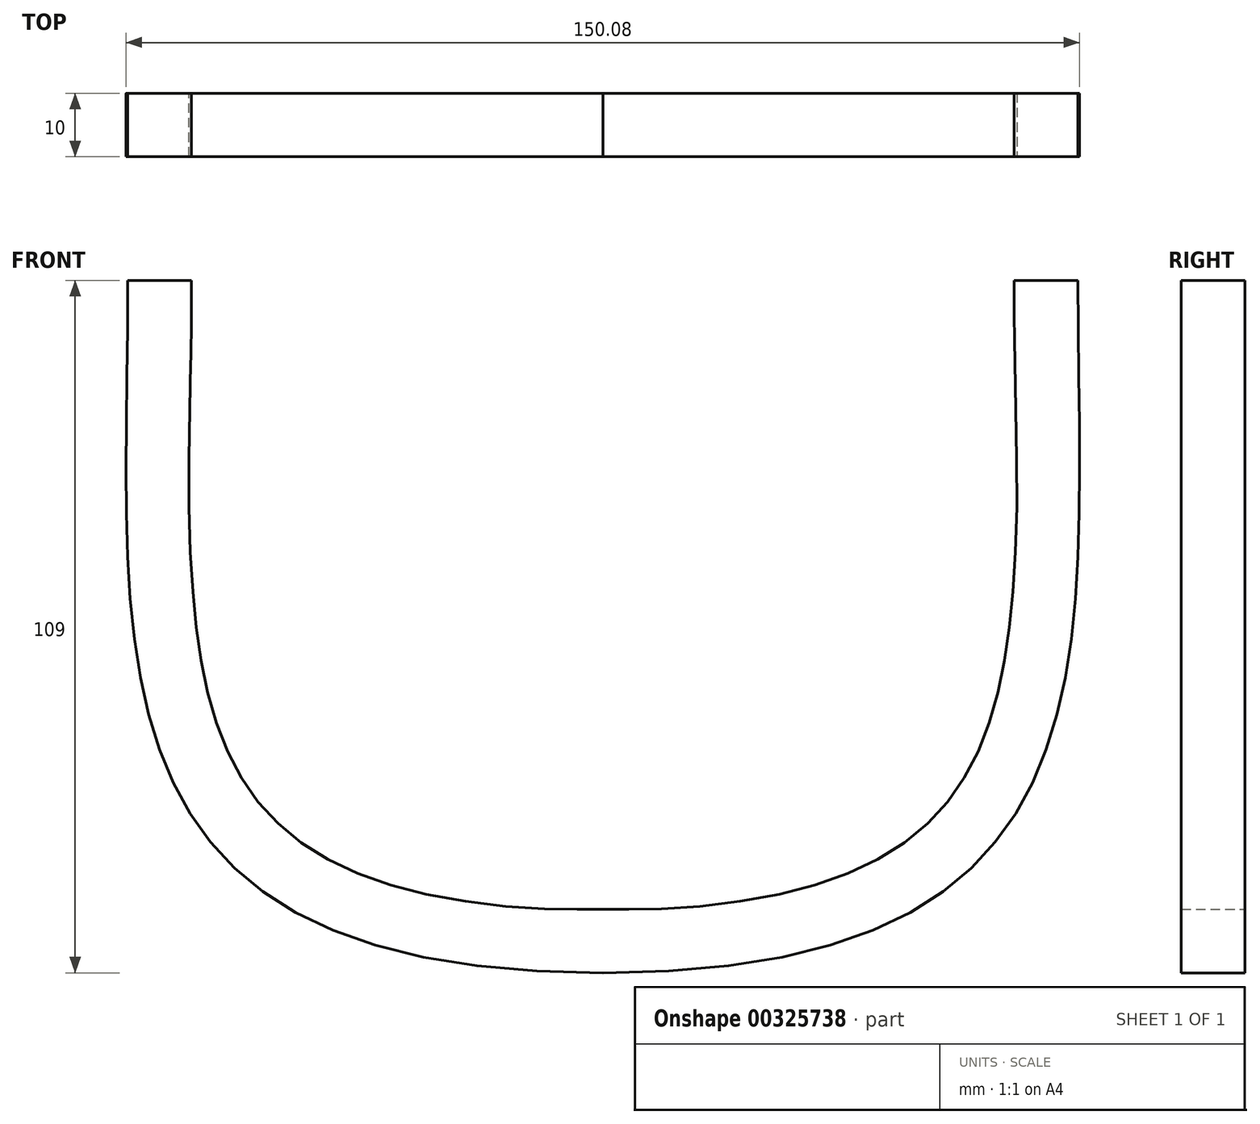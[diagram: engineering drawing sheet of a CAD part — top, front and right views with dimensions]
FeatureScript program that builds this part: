
annotation { "Feature Type Name" : "Feature", "Feature Type Description" : "" }
export const myFeature = defineFeature(function(context is Context, id is Id, definition is map)
    precondition{}
    {
        {
            var Q0;
            Q0=qCreatedBy(makeId("Front.planeOp"),FACE);
            var sketch = newSketch(context, id + "F0", { "sketchPlane" : qUnion([Q0])});
            skLineSegment(sketch, "E0", {"start": v(-75.24, 0) * mm, "end": v(74.76, 0) * mm, "construction": true});
            skLineSegment(sketch, "E1", {"start": v(74.76, 0) * mm, "end": v(74.76, 109) * mm, "construction": true});
            skLineSegment(sketch, "E2", {"start": v(0, 0) * mm, "end": v(0, 109) * mm, "construction": true});
            skFitSpline(sketch, "E3", {"points": [v(0, 0) * mm, v(74.76, 109) * mm], "startDerivative": vector(251, 0) * mm, "endDerivative": vector(0, 176.06) * mm});
            skFitSpline(sketch, "E4.MirrorCS", {"points": [v(0, 0) * mm, v(-74.76, 109) * mm], "startDerivative": vector(-251, 0) * mm, "endDerivative": vector(0, 176.06) * mm});
            skFitSpline(sketch, "E5.0", {"points": [v(0, 10) * mm, v(-4.98, 10) * mm, v(-14.16, 10.37) * mm, v(-25.7, 11.95) * mm, v(-35.14, 14.4) * mm, v(-42.67, 17.57) * mm, v(-48.55, 21.31) * mm, v(-53.13, 25.58) * mm, v(-56.75, 30.48) * mm, v(-59.63, 36.16) * mm, v(-61.82, 42.74) * mm, v(-63.4, 50.2) * mm, v(-64.4, 58.47) * mm, v(-65.09, 70.47) * mm, v(-65.04, 87.04) * mm, v(-64.76, 101.54) * mm, v(-64.76, 109) * mm]});
            skFitSpline(sketch, "E6.0", {"points": [v(0, 10) * mm, v(4.98, 10) * mm, v(14.16, 10.37) * mm, v(25.7, 11.95) * mm, v(35.14, 14.4) * mm, v(42.67, 17.57) * mm, v(48.55, 21.31) * mm, v(53.13, 25.58) * mm, v(56.75, 30.48) * mm, v(59.63, 36.16) * mm, v(61.82, 42.74) * mm, v(63.4, 50.2) * mm, v(64.4, 58.47) * mm, v(65.09, 70.47) * mm, v(65.04, 87.04) * mm, v(64.76, 101.54) * mm, v(64.76, 109) * mm]});
            skLineSegment(sketch, "E7", {"start": v(-74.76, 109) * mm, "end": v(-64.76, 109) * mm});
            skLineSegment(sketch, "E8", {"start": v(64.76, 109) * mm, "end": v(74.76, 109) * mm});
            skPoint(sketch, "E9", {"position": v(-64.77, 106.13) * mm});
            skPoint(sketch, "E10", {"position": v(-64.87, 96.13) * mm});
            skPoint(sketch, "E11", {"position": v(64.77, 106.13) * mm});
            skPoint(sketch, "E12", {"position": v(64.87, 96.13) * mm});
            skPoint(sketch, "E13", {"position": v(-46.66, 96.13) * mm});
            skPoint(sketch, "E14", {"position": v(-65.02, 82.6) * mm});
            skPoint(sketch, "E15", {"position": v(65.02, 82.6) * mm});
            skPoint(sketch, "E16", {"position": v(46.66, 96.13) * mm});
            skLineSegment(sketch, "E17", {"start": v(-64.87, 96.13) * mm, "end": v(-46.66, 96.13) * mm});
            skLineSegment(sketch, "E18", {"start": v(-65.02, 82.6) * mm, "end": v(-46.66, 96.13) * mm});
            skLineSegment(sketch, "E19", {"start": v(46.66, 96.13) * mm, "end": v(65.02, 82.6) * mm});
            skLineSegment(sketch, "E20", {"start": v(46.66, 96.13) * mm, "end": v(64.87, 96.13) * mm});
            skSolve(sketch);
        }
        {
            var Q0;
            Q0 = qSketchRegion(id + "F0", true);
            extrude(context, id + "F1", {"entities" : qUnion([Q0]), "endBound" : BoundingType.SYMMETRIC, "depth" : 10 * mm});
        }
    });
